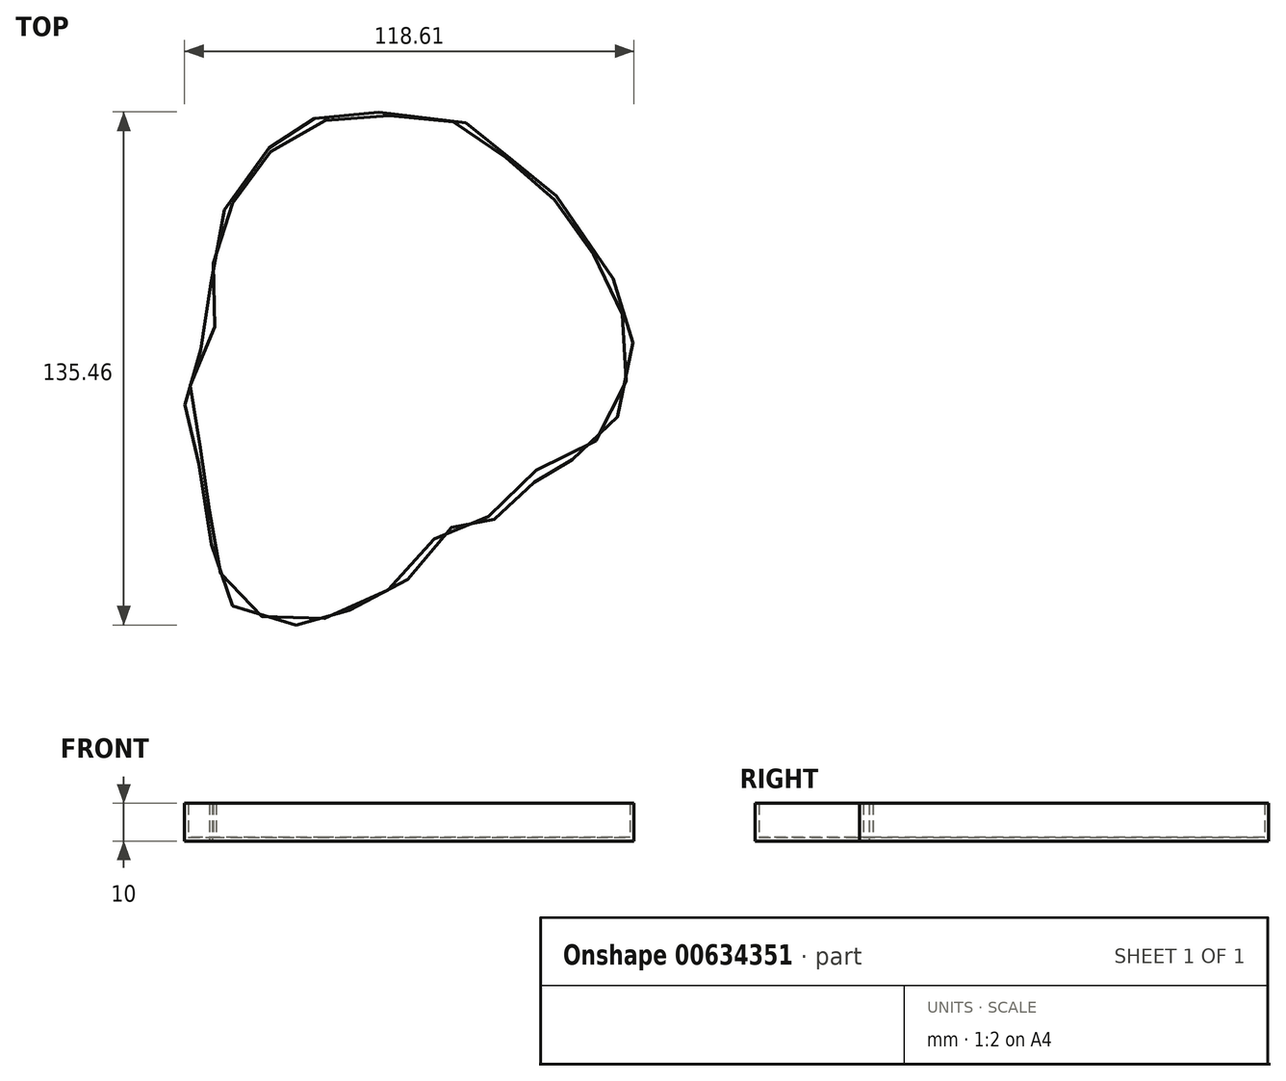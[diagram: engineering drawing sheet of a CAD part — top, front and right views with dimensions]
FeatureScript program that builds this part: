
annotation { "Feature Type Name" : "Feature", "Feature Type Description" : "" }
export const myFeature = defineFeature(function(context is Context, id is Id, definition is map)
    precondition{}
    {
        {
            var Q0;
            Q0=qCreatedBy(makeId("Top.planeOp"),FACE);
            var sketch = newSketch(context, id + "F0", { "sketchPlane" : qUnion([Q0])});
            skFitSpline(sketch, "E0", {"points": [v(20.43, 70.58) * mm, v(27.49, 65.41) * mm, v(32.55, 61.14) * mm, v(33.94, 58.26) * mm, v(38.41, 56.57) * mm, v(51.13, 42.07) * mm, v(60.46, 27.17) * mm, v(63.11, 18.87) * mm, v(64.82, 8.97) * mm, v(61.77, -3.83) * mm, v(58.05, -11.34) * mm, v(51.3, -17.16) * mm, v(44.41, -19.41) * mm, v(41.03, -20.16) * mm, v(38.72, -23.92) * mm, v(34.15, -29.86) * mm, v(29.52, -33.24) * mm, v(26.2, -34.37) * mm, v(22.53, -31.92) * mm, v(16.37, -36.53) * mm, v(10.64, -42.34) * mm, v(3.76, -51.26) * mm, v(-4.48, -55.71) * mm, v(-11.74, -58.78) * mm, v(-16.48, -61.2) * mm, v(-24.17, -62) * mm, v(-32.11, -61.1) * mm, v(-41.63, -56.31) * mm, v(-45.65, -46.58) * mm, v(-46.82, -39.73) * mm, v(-49.07, -26.53) * mm, v(-51, -13.17) * mm, v(-52.66, -7.54) * mm, v(-53.71, -0.8) * mm, v(-51.03, 6.93) * mm, v(-49, 11.82) * mm, v(-46.53, 18.32) * mm, v(-47.2, 30.63) * mm, v(-45.03, 43.62) * mm, v(-39.71, 53.25) * mm, v(-31.78, 63.64) * mm, v(-26.03, 68.33) * mm, v(-21.17, 71.1) * mm, v(-17.5, 72.05) * mm, v(-11.14, 72.72) * mm, v(6.57, 73.4) * mm, v(20.43, 70.58) * mm]});
            skSolve(sketch);
        }
        {
            var Q0;
            Q0=makeQuery(id+"F0.imprint","IMPRINT",FACE,{"disambiguationData":[TD([[makeQuery(id+"F0.imprint","IMPRINT",EDGE,{"derivedFrom":sQuery(id+"F0.wireOp",EDGE,"E0")}),-1.0]])]});
            extrude(context, id + "F1", {"entities" : qUnion([Q0]), "depth" : 10 * mm, "offsetDistance" : 25 * mm});
        }
        {
            var Q0;
            Q0=makeQuery(id+"F1.opExtrude","CAP_FACE",FACE,{"disambiguationData":[OSD([sQuery(id+"F0.wireOp",EDGE,"E0")])],"isStart":false});
            shell(context, id + "F2", {"entities" : qUnion([Q0]), "thickness" : 1 * mm});
        }
        {
            var Q0;
            Q0=qCreatedBy(makeId("Top.planeOp"),FACE);
            var sketch = newSketch(context, id + "F3", { "sketchPlane" : qUnion([Q0])});
            skFitSpline(sketch, "E1", {"points": [v(-44.77, 19.9) * mm, v(-41.4, 27.43) * mm, v(-38.3, 37.52) * mm, v(-35.6, 45.1) * mm, v(-31.05, 50.98) * mm, v(-26.56, 54.26) * mm, v(-15.08, 55.95) * mm, v(-7.07, 56.64) * mm, v(13.83, 50.35) * mm, v(22.27, 46.14) * mm, v(30.24, 42.85) * mm, v(35.22, 32.04) * mm, v(34.27, 18.22) * mm, v(31.9, 15.74) * mm, v(31.08, 6.4) * mm, v(29.55, -1.39) * mm, v(24.7, -13.2) * mm, v(26.48, -15.2) * mm, v(25.77, -12.85) * mm, v(30.26, -1.62) * mm, v(31.9, 6.64) * mm, v(32.62, 15.27) * mm, v(34.98, 17.51) * mm, v(36.28, 32.4) * mm, v(30.73, 43.74) * mm, v(22.58, 46.93) * mm, v(14.25, 51.03) * mm, v(-6.88, 57.26) * mm, v(-15.08, 56.63) * mm, v(-26.75, 54.97) * mm, v(-31.71, 51.43) * mm, v(-36.29, 45.28) * mm, v(-38.74, 37.57) * mm, v(-41.75, 27.56) * mm, v(-44.77, 19.9) * mm]});
            skSolve(sketch);
        }
        {
            var Q0;
            Q0=sQuery(id+"F3.wireOp",EDGE,"E1");
            extrude(context, id + "F4", {"bodyType" : ToolBodyType.SURFACE, "surfaceEntities" : qUnion([Q0]), "depth" : 5 * mm, "offsetDistance" : 25 * mm});
        }
        {
            var Q0;
            Q0=qCreatedBy(makeId("Top.planeOp"),FACE);
            var sketch = newSketch(context, id + "F5", { "sketchPlane" : qUnion([Q0])});
            skFitSpline(sketch, "E2", {"points": [v(22.78, -30.74) * mm, v(25.2, -24.3) * mm, v(26.44, -15.62) * mm, v(31, -10.54) * mm, v(39.8, -6.35) * mm, v(40.32, -11.3) * mm, v(39.85, -15.68) * mm, v(40.56, -18.75) * mm, v(40.8, -18.63) * mm, v(40.26, -15.56) * mm, v(40.8, -11.37) * mm, v(40.15, -6) * mm, v(30.76, -10.19) * mm, v(25.97, -15.5) * mm, v(24.79, -24.19) * mm, v(22.78, -30.74) * mm]});
            skSolve(sketch);
        }
        {
            var Q0;
            Q0=sQuery(id+"F5.wireOp",EDGE,"E2");
            extrude(context, id + "F6", {"bodyType" : ToolBodyType.SURFACE, "surfaceEntities" : qUnion([Q0]), "depth" : 5 * mm, "offsetDistance" : 25 * mm});
        }
        {
            var Q0;
            Q0=qCreatedBy(makeId("Top.planeOp"),FACE);
            var sketch = newSketch(context, id + "F7", { "sketchPlane" : qUnion([Q0])});
            skFitSpline(sketch, "E3", {"points": [v(-35.9, 21.84) * mm, v(-33.52, 23.03) * mm, v(-28.3, 21.99) * mm, v(-24.14, 17.9) * mm, v(-24.8, 14.25) * mm, v(-28.6, 12.16) * mm, v(-35.38, 14.02) * mm, v(-36.64, 17.67) * mm, v(-35.9, 21.84) * mm]});
            skFitSpline(sketch, "E4", {"points": [v(-5.27, 4.33) * mm, v(-2.89, 5.52) * mm, v(2.32, 4.47) * mm, v(6.49, 0.38) * mm, v(5.82, -3.27) * mm, v(2.02, -5.35) * mm, v(-4.75, -3.49) * mm, v(-6.01, 0.16) * mm, v(-5.27, 4.33) * mm]});
            skSolve(sketch);
        }
        {
            var Q0;
            Q0=sQuery(id+"F7.wireOp",EDGE,"E3");
            extrude(context, id + "F8", {"bodyType" : ToolBodyType.SURFACE, "surfaceEntities" : qUnion([Q0]), "depth" : 5 * mm, "offsetDistance" : 25 * mm});
        }
        {
            var Q0;
            Q0=qCreatedBy(makeId("Top.planeOp"),FACE);
            var sketch = newSketch(context, id + "F9", { "sketchPlane" : qUnion([Q0])});
            skFitSpline(sketch, "E5", {"points": [v(-39.16, 28.6) * mm, v(-36.97, 30.98) * mm, v(-33.72, 32.18) * mm, v(-25.17, 29.72) * mm, v(-19.27, 22.76) * mm, v(-19.14, 21.7) * mm, v(-20.86, 22.23) * mm, v(-27.49, 26.68) * mm, v(-34.72, 28.93) * mm, v(-39.16, 28.6) * mm]});
            skSolve(sketch);
        }
        {
            var Q0;
            Q0=sQuery(id+"F9.wireOp",EDGE,"E5");
            extrude(context, id + "F10", {"bodyType" : ToolBodyType.SURFACE, "surfaceEntities" : qUnion([Q0]), "depth" : 5 * mm, "offsetDistance" : 25 * mm});
        }
        {
            var Q0;
            Q0=qCreatedBy(makeId("Top.planeOp"),FACE);
            var sketch = newSketch(context, id + "F11", { "sketchPlane" : qUnion([Q0])});
            skFitSpline(sketch, "E6", {"points": [v(-3.84, 13.86) * mm, v(0, 14.31) * mm, v(6.81, 12.27) * mm, v(10.67, 8.2) * mm, v(5, 3.43) * mm, v(-3.16, 3.88) * mm, v(-5.2, 9.55) * mm, v(-3.84, 13.86) * mm]});
            skSolve(sketch);
        }
        {
            var Q0;
            Q0=sQuery(id+"F11.wireOp",EDGE,"E6");
            extrude(context, id + "F12", {"bodyType" : ToolBodyType.SURFACE, "surfaceEntities" : qUnion([Q0]), "depth" : 5 * mm, "offsetDistance" : 25 * mm});
        }
        {
            var Q0;
            Q0=qCreatedBy(makeId("Top.planeOp"),FACE);
            var sketch = newSketch(context, id + "F13", { "sketchPlane" : qUnion([Q0])});
            skFitSpline(sketch, "E7", {"points": [v(-4.23, 19.25) * mm, v(0, 21.27) * mm, v(3.34, 20.77) * mm, v(8.7, 19.05) * mm, v(14.35, 15.31) * mm, v(17.48, 9.66) * mm, v(13.84, 11.88) * mm, v(4.45, 17.23) * mm, v(-4.23, 19.25) * mm]});
            skSolve(sketch);
        }
        {
            var Q0;
            Q0=sQuery(id+"F13.wireOp",EDGE,"E7");
            extrude(context, id + "F14", {"bodyType" : ToolBodyType.SURFACE, "surfaceEntities" : qUnion([Q0]), "depth" : 5 * mm, "offsetDistance" : 25 * mm});
        }
        {
            var Q0;
            Q0=qCreatedBy(makeId("Top.planeOp"),FACE);
            var sketch = newSketch(context, id + "F15", { "sketchPlane" : qUnion([Q0])});
            skFitSpline(sketch, "E8", {"points": [v(-19.16, 8.53) * mm, v(-21.07, 3.24) * mm, v(-24.55, -3.51) * mm, v(-27.27, -7.04) * mm, v(-27.32, -10.12) * mm, v(-27.07, -7.04) * mm, v(-24.35, -3.66) * mm, v(-20.77, 3.24) * mm, v(-19.16, 8.53) * mm]});
            skSolve(sketch);
        }
        {
            var Q0;
            Q0=sQuery(id+"F15.wireOp",EDGE,"E8");
            extrude(context, id + "F16", {"bodyType" : ToolBodyType.SURFACE, "surfaceEntities" : qUnion([Q0]), "depth" : 5 * mm, "offsetDistance" : 25 * mm});
        }
        {
            var Q0;
            Q0=qCreatedBy(makeId("Top.planeOp"),FACE);
            var sketch = newSketch(context, id + "F17", { "sketchPlane" : qUnion([Q0])});
            skFitSpline(sketch, "E9", {"points": [v(-35.95, -22.65) * mm, v(-33.3, -23.72) * mm, v(-28.88, -25.79) * mm, v(-23.3, -27.07) * mm, v(-17.74, -27.79) * mm, v(-12.03, -28.79) * mm, v(-11.82, -30.93) * mm, v(-15.24, -33.86) * mm, v(-22.17, -35.36) * mm, v(-28.6, -35) * mm, v(-33.95, -31.14) * mm, v(-38.02, -26) * mm, v(-35.95, -22.65) * mm]});
            skSolve(sketch);
        }
        {
            var Q0;
            Q0=sQuery(id+"F17.wireOp",EDGE,"E9");
            extrude(context, id + "F18", {"bodyType" : ToolBodyType.SURFACE, "surfaceEntities" : qUnion([Q0]), "depth" : 5 * mm, "offsetDistance" : 25 * mm});
        }
        {
            var Q0;
            Q0=qCreatedBy(makeId("Top.planeOp"),FACE);
            var sketch = newSketch(context, id + "F19", { "sketchPlane" : qUnion([Q0])});
            skFitSpline(sketch, "E10", {"points": [v(-33.52, -28.64) * mm, v(-30.16, -30.21) * mm, v(-25.02, -31.36) * mm, v(-16.96, -31.93) * mm, v(-25.1, -31) * mm, v(-29.88, -29.79) * mm, v(-33.52, -28.64) * mm]});
            skSolve(sketch);
        }
        {
            var Q0;
            Q0=sQuery(id+"F19.wireOp",EDGE,"E10");
            extrude(context, id + "F20", {"bodyType" : ToolBodyType.SURFACE, "surfaceEntities" : qUnion([Q0]), "depth" : 5 * mm, "offsetDistance" : 25 * mm});
        }
    });
